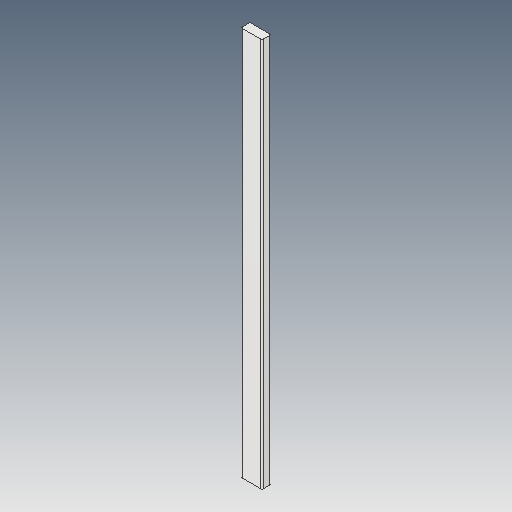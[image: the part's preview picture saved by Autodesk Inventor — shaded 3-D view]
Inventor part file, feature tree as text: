
AUTODESK INVENTOR PART (.ipt)
format: ipt  version: 2023.5 (Build 275446000, 446)  size: 82,944 bytes
history: native  units: in
note: dims shown in document units (in); Inventor stores cm internally (conversion verified against a paired STEP export)
features: fillet x1
ambient origin geometry x8: Origin, YZ Plane, XZ Plane, XY Plane, X Axis, Y Axis, Z Axis, Center Point
bodies: Solid1 (feature_tree)
feature tree (1):
  fillet  "Fillet1"  [1 undecoded]
note: 1 required parameter value undecoded (feature->parameter linkage not recoverable at this tier; creation-order binding heuristic only, values carry confidence <= 0.55)
